# Revit family: Trim
name_source: partatom
category: Mobiliario
revit_build: Autodesk Revit 2016 (Build: 20150220_1215(x64)
units: mm (PartAtom-declared; Revit-internal decimal feet)

## family parameters
Compartido = No
Corte con vacíos al cargar = No
Número OmniClass = 23.40.20.00
Punto de cálculo de habitación = No
Se basa en plano de trabajo = No
Siempre vertical = Sí
Título OmniClass = General Furniture and Specialties

## types (4) — shared parameters
Armrest Material = Black Polypropylene
Back Height = 52 cm
Base Height = 36 cm
Chair Parts Material = Black Polypropylene
Código de montaje = E2020200
Fabricante = ACTIU
Seat Height = 53 cm
Total Height = 105 cm
URL = www.actiu.com
URL Producto = https://www.actiu.com

## per-type parameters (varying)
| type | Armest Frame | Armrest | Back Material | Back Material_02 | Catálogo Producto | Certificados | Chair Base Material | Chair Frame Material | Comentarios de tipo | Descripción | Modelo | No Armrest | Seat Material |
| No Armrest | White | No | UpholsteredT:86 | Black Polypropylene | https://www.actiu.com |  | Black Aluminum | Black |  | Task chair - Synchronised tilting | TNK Flex _Mid-Back | Sí | UpholsteredT:86 |
| Armrest | White | Sí | Melange:76(EN) | Black Polypropylene | https://actiucdn.net | https://actiucdn.net | White Aluminum | White | 48/53 x 94/113 cm | Trim is a versatile, ergonomic and flexible chair | TRIM | No | Melange:76(EN) |
| Armrest_T | Black | Sí | UpholsteredT:91 | UpholsteredT:91 | https://actiucdn.net | https://actiucdn.net | White Aluminum | White | 48/53 x 94/113 cm | Trim is a versatile, ergonomic and flexible chair | TRIM | No | UpholsteredT:91 |
| No Armrest_Leather | White | No | Leather:18 | Leather:18 | https://www.actiu.com |  | Black Aluminum | Black |  | Task chair - Synchronised tilting | TNK Flex _Mid-Back | Sí | Leather:18 |

## geometry (parser evidence)
native form markers: Blend x3
no freeform markers — native parametric forms only
